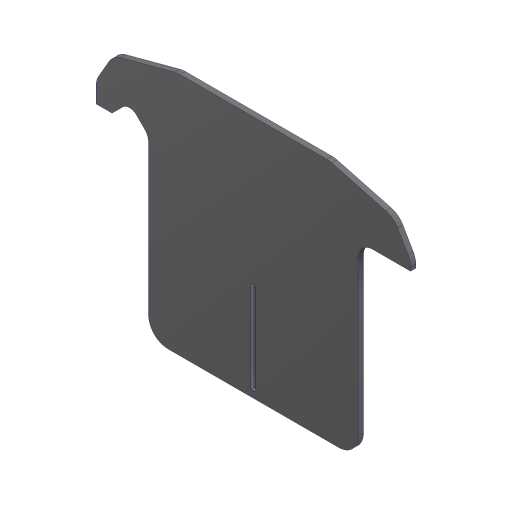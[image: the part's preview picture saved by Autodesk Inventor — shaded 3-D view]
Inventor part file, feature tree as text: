
AUTODESK INVENTOR PART (.ipt)
format: ipt  version: 2023 (Build 270158000, 158)  size: 553,984 bytes
history: native  units: mm
features: extrude x1, sketch x1, other x1
ambient origin geometry x8: Origin, YZ Plane, XZ Plane, XY Plane, X Axis, Y Axis, Z Axis, Center Point
bodies: Solid1 (feature_tree)
feature tree (3):
  extrude  "Extrusion1"  Depth=22.0mm
  sketch  "Sketch1"  dims[d0=1.1mm d1=22.0mm d2=0.0mm d3=0.0mm]
  other  "16588-001-1-solid1"
